# Revit family: 875-00-001-DN200-1200
name_source: partatom
category: Pipe Accessories
units: mm (PartAtom-declared; Revit-internal decimal feet)

## family parameters
Always vertical = Yes
Cut with Voids When Loaded = No
Part Type = Valve - Breaks Into
Round Connector Dimension = Use Diameter
Shared = No
Work Plane-Based = No

## types (26) — shared parameters
875-0200-00-03100000 = DN200_PN10
875-0200-00-13100000 = DN200_PN16
875-0250-00-03100000 = DN250_PN10
875-0250-00-13100000 = DN250_PN16
875-0300-00-03100000 = DN300_PN10
875-0300-00-13100000 = DN300_PN16
875-0350-00-03100000 = DN350_PN10
875-0350-00-13100000 = DN350_PN16
875-0400-00-03100000 = DN400_PN10
875-0400-00-13100000 = DN400_PN16
875-0450-00-03100000 = DN450_PN10
875-0450-00-13100000 = DN450_PN16
875-0500-00-03100000 = DN500_PN10
875-0500-00-13100000 = DN500_PN16
875-0600-00-03100000 = DN600_PN10
875-0600-00-13100000 = DN600_PN16
875-0700-00-03100000 = DN700_PN10
875-0700-00-13100000 = DN700_PN16
875-0800-00-03100000 = DN800_PN10
875-0800-00-13100000 = DN800_PN16
875-0900-00-03100000 = DN900_PN10
875-0900-00-13100000 = DN900_PN16
875-1000-00-03100000 = DN1000_PN10
875-1000-00-13100000 = DN1000_PN16
875-1200-00-03100000 = DN1200_PN10
875-1200-00-13100000 = DN1200_PN16
Body_Wallthickness = 10 mm  [stored 0.0328084 ft]
Description_ = AVK TILTING DISC, SLANTED CHECK VALVE
Rf_Dia = 3 mm  [stored 0.00984252 ft]
Search_Table = 875-00-001-DN200-1200
URL product pages = https://www.avkvalves.com

## per-type parameters (varying)
- DN0200_PN10: A=161 mm; B=202 mm; C=525 mm; Counter_weight=105 mm  [stored 0.344488 ft]; D=170 mm; D2=133 mm; DN=200 mm; DN_ref=174 mm; Disc_dia=165 mm; Disc_dia_ref=83 mm; Flange_Thickness=15 mm  [stored 0.0492126 ft]; H=460 mm; H3=345 mm; H_ref=290 mm; H_ref_2=193 mm; ID=100 mm  [stored 0.328084 ft]; ID_ref=100 mm  [stored 0.328084 ft]; L=230 mm; L1=55 mm  [stored 0.180446 ft]; L_ref=66 mm  [stored 0.216535 ft]; L_ref_2=60 mm  [stored 0.19685 ft]; L_ref_3=46 mm  [stored 0.150919 ft]; L_ref_4=66 mm  [stored 0.216535 ft]; Lever=30 mm  [stored 0.0984252 ft]; Pin=10 mm  [stored 0.0328084 ft]
- DN0200_PN16: A=161 mm; B=202 mm; C=525 mm; Counter_weight=105 mm  [stored 0.344488 ft]; D=170 mm; D2=133 mm; DN=200 mm; DN_ref=174 mm; Disc_dia=165 mm; Disc_dia_ref=83 mm; Flange_Thickness=15 mm  [stored 0.0492126 ft]; H=460 mm; H3=345 mm; H_ref=290 mm; H_ref_2=193 mm; ID=100 mm  [stored 0.328084 ft]; ID_ref=100 mm  [stored 0.328084 ft]; L=230 mm; L1=55 mm  [stored 0.180446 ft]; L_ref=66 mm  [stored 0.216535 ft]; L_ref_2=60 mm  [stored 0.19685 ft]; L_ref_3=46 mm  [stored 0.150919 ft]; L_ref_4=66 mm  [stored 0.216535 ft]; Lever=30 mm  [stored 0.0984252 ft]; Pin=10 mm  [stored 0.0328084 ft]
- DN0250_PN10: A=202 mm; B=230 mm; C=583 mm; Counter_weight=105 mm  [stored 0.344488 ft]; D=198 mm; D2=160 mm; DN=250 mm; DN_ref=217 mm; Disc_dia=210 mm; Disc_dia_ref=105 mm  [stored 0.344488 ft]; Flange_Thickness=15 mm  [stored 0.0492126 ft]; H=512 mm; H3=403 mm; H_ref=315 mm; H_ref_2=210 mm; ID=125 mm; ID_ref=125 mm; L=250 mm; L1=75 mm  [stored 0.246063 ft]; L_ref=71 mm; L_ref_2=65 mm; L_ref_3=50 mm  [stored 0.164042 ft]; L_ref_4=71 mm; Lever=30 mm  [stored 0.0984252 ft]; Pin=10 mm  [stored 0.0328084 ft]
- DN0250_PN16: A=202 mm; B=230 mm; C=583 mm; Counter_weight=105 mm  [stored 0.344488 ft]; D=203 mm; D2=160 mm; DN=250 mm; DN_ref=217 mm; Disc_dia=210 mm; Disc_dia_ref=105 mm  [stored 0.344488 ft]; Flange_Thickness=15 mm  [stored 0.0492126 ft]; H=512 mm; H3=408 mm; H_ref=310 mm; H_ref_2=206 mm; ID=125 mm; ID_ref=125 mm; L=250 mm; L1=75 mm  [stored 0.246063 ft]; L_ref=71 mm; L_ref_2=65 mm; L_ref_3=50 mm  [stored 0.164042 ft]; L_ref_4=71 mm; Lever=30 mm  [stored 0.0984252 ft]; Pin=10 mm  [stored 0.0328084 ft]
- DN0300_PN10: A=220 mm; B=265 mm; C=667 mm; Counter_weight=140 mm; D=223 mm; D2=185 mm; DN=300 mm; DN_ref=261 mm; Disc_dia=250 mm; Disc_dia_ref=125 mm; Flange_Thickness=20 mm  [stored 0.0656168 ft]; H=637 mm; H3=455 mm; H_ref=415 mm; H_ref_2=276 mm; ID=150 mm; ID_ref=150 mm; L=270 mm; L1=100 mm  [stored 0.328084 ft]; L_ref=77 mm; L_ref_2=70 mm  [stored 0.229659 ft]; L_ref_3=54 mm  [stored 0.177165 ft]; L_ref_4=77 mm; Lever=40 mm  [stored 0.131234 ft]; Pin=15 mm  [stored 0.0492126 ft]
- DN0300_PN16: A=220 mm; B=265 mm; C=667 mm; Counter_weight=140 mm; D=230 mm; D2=185 mm; DN=300 mm; DN_ref=261 mm; Disc_dia=250 mm; Disc_dia_ref=125 mm; Flange_Thickness=20 mm  [stored 0.0656168 ft]; H=637 mm; H3=462 mm; H_ref=407 mm; H_ref_2=271 mm; ID=150 mm; ID_ref=150 mm; L=270 mm; L1=100 mm  [stored 0.328084 ft]; L_ref=77 mm; L_ref_2=70 mm  [stored 0.229659 ft]; L_ref_3=54 mm  [stored 0.177165 ft]; L_ref_4=77 mm; Lever=40 mm  [stored 0.131234 ft]; Pin=15 mm  [stored 0.0492126 ft]
- DN0350_PN10: A=245 mm; B=300 mm; C=728 mm; Counter_weight=140 mm; D=253 mm; D2=215 mm; DN=350 mm; DN_ref=304 mm; Disc_dia=290 mm; Disc_dia_ref=145 mm; Flange_Thickness=20 mm  [stored 0.0656168 ft]; H=676 mm; H3=518 mm; H_ref=424 mm; H_ref_2=282 mm; ID=175 mm; ID_ref=175 mm; L=290 mm; L1=135 mm; L_ref=83 mm; L_ref_2=75 mm  [stored 0.246063 ft]; L_ref_3=58 mm  [stored 0.190289 ft]; L_ref_4=83 mm; Lever=40 mm  [stored 0.131234 ft]; Pin=15 mm  [stored 0.0492126 ft]
- DN0350_PN16: A=245 mm; B=300 mm; C=728 mm; Counter_weight=140 mm; D=260 mm; D2=215 mm; DN=350 mm; DN_ref=304 mm; Disc_dia=290 mm; Disc_dia_ref=145 mm; Flange_Thickness=20 mm  [stored 0.0656168 ft]; H=676 mm; H3=525 mm; H_ref=416 mm; H_ref_2=277 mm; ID=175 mm; ID_ref=175 mm; L=290 mm; L1=135 mm; L_ref=83 mm; L_ref_2=75 mm  [stored 0.246063 ft]; L_ref_3=58 mm  [stored 0.190289 ft]; L_ref_4=83 mm; Lever=40 mm  [stored 0.131234 ft]; Pin=15 mm  [stored 0.0492126 ft]
- DN0400_PN10: A=270 mm; B=345 mm; C=867 mm; Counter_weight=140 mm; D=283 mm; D2=240 mm; DN=400 mm; DN_ref=348 mm; Disc_dia=335 mm; Disc_dia_ref=168 mm; Flange_Thickness=20 mm  [stored 0.0656168 ft]; H=719 mm; H3=578 mm; H_ref=437 mm; H_ref_2=291 mm; ID=200 mm; ID_ref=200 mm; L=310 mm; L1=150 mm; L_ref=89 mm; L_ref_2=81 mm; L_ref_3=62 mm  [stored 0.203412 ft]; L_ref_4=89 mm; Lever=40 mm  [stored 0.131234 ft]; Pin=15 mm  [stored 0.0492126 ft]
- DN0400_PN16: A=270 mm; B=345 mm; C=867 mm; Counter_weight=140 mm; D=290 mm; D2=240 mm; DN=400 mm; DN_ref=348 mm; Disc_dia=335 mm; Disc_dia_ref=168 mm; Flange_Thickness=20 mm  [stored 0.0656168 ft]; H=719 mm; H3=585 mm; H_ref=429 mm; H_ref_2=286 mm; ID=200 mm; ID_ref=200 mm; L=310 mm; L1=150 mm; L_ref=89 mm; L_ref_2=81 mm; L_ref_3=62 mm  [stored 0.203412 ft]; L_ref_4=89 mm; Lever=40 mm  [stored 0.131234 ft]; Pin=15 mm  [stored 0.0492126 ft]
- DN0450_PN10: A=330 mm; B=378 mm; C=963 mm; Counter_weight=210 mm; D=308 mm; D2=265 mm; DN=450 mm; DN_ref=391 mm; Disc_dia=370 mm; Disc_dia_ref=185 mm; Flange_Thickness=30 mm  [stored 0.0984252 ft]; H=751 mm; H3=620 mm; H_ref=444 mm; H_ref_2=296 mm; ID=225 mm; ID_ref=225 mm; L=330 mm; L1=190 mm; L_ref=94 mm  [stored 0.308399 ft]; L_ref_2=86 mm  [stored 0.282152 ft]; L_ref_3=66 mm  [stored 0.216535 ft]; L_ref_4=94 mm  [stored 0.308399 ft]; Lever=60 mm  [stored 0.19685 ft]; Pin=25 mm  [stored 0.082021 ft]
- DN0450_PN16: A=330 mm; B=378 mm; C=963 mm; Counter_weight=210 mm; D=320 mm; D2=274 mm; DN=450 mm; DN_ref=391 mm; Disc_dia=370 mm; Disc_dia_ref=185 mm; Flange_Thickness=30 mm  [stored 0.0984252 ft]; H=751 mm; H3=645 mm; H_ref=431 mm; H_ref_2=287 mm; ID=225 mm; ID_ref=225 mm; L=330 mm; L1=190 mm; L_ref=94 mm  [stored 0.308399 ft]; L_ref_2=86 mm  [stored 0.282152 ft]; L_ref_3=66 mm  [stored 0.216535 ft]; L_ref_4=94 mm  [stored 0.308399 ft]; Lever=60 mm  [stored 0.19685 ft]; Pin=25 mm  [stored 0.082021 ft]
- DN0500_PN10: A=370 mm; B=405 mm; C=1006 mm; Counter_weight=210 mm; D=335 mm; D2=291 mm; DN=500 mm; DN_ref=435 mm; Disc_dia=410 mm; Disc_dia_ref=205 mm; Flange_Thickness=30 mm  [stored 0.0984252 ft]; H=809 mm; H3=675 mm; H_ref=474 mm; H_ref_2=316 mm; ID=250 mm; ID_ref=250 mm; L=350 mm; L1=210 mm; L_ref=100 mm  [stored 0.328084 ft]; L_ref_2=91 mm; L_ref_3=70 mm  [stored 0.229659 ft]; L_ref_4=100 mm  [stored 0.328084 ft]; Lever=60 mm  [stored 0.19685 ft]; Pin=25 mm  [stored 0.082021 ft]
- DN0500_PN16: A=370 mm; B=405 mm; C=1006 mm; Counter_weight=210 mm; D=358 mm; D2=305 mm; DN=500 mm; DN_ref=435 mm; Disc_dia=410 mm; Disc_dia_ref=205 mm; Flange_Thickness=30 mm  [stored 0.0984252 ft]; H=809 mm; H3=720 mm; H_ref=452 mm; H_ref_2=301 mm; ID=250 mm; ID_ref=250 mm; L=350 mm; L1=210 mm; L_ref=100 mm  [stored 0.328084 ft]; L_ref_2=91 mm; L_ref_3=70 mm  [stored 0.229659 ft]; L_ref_4=100 mm  [stored 0.328084 ft]; Lever=60 mm  [stored 0.19685 ft]; Pin=25 mm  [stored 0.082021 ft]
- DN0600_PN10: A=395 mm; B=465 mm; C=1180 mm; Counter_weight=210 mm; D=390 mm; D2=341 mm; DN=600 mm; DN_ref=522 mm; Disc_dia=500 mm; Disc_dia_ref=250 mm; Flange_Thickness=30 mm  [stored 0.0984252 ft]; H=1096 mm; H3=785 mm; H_ref=706 mm; H_ref_2=471 mm; ID=300 mm; ID_ref=300 mm; L=390 mm; L1=265 mm; L_ref=111 mm; L_ref_2=101 mm; L_ref_3=78 mm  [stored 0.255906 ft]; L_ref_4=111 mm; Lever=60 mm  [stored 0.19685 ft]; Pin=25 mm  [stored 0.082021 ft]
- DN0600_PN16: A=395 mm; B=465 mm; C=1180 mm; Counter_weight=210 mm; D=420 mm; D2=360 mm; DN=600 mm; DN_ref=522 mm; Disc_dia=500 mm; Disc_dia_ref=250 mm; Flange_Thickness=30 mm  [stored 0.0984252 ft]; H=1096 mm; H3=845 mm; H_ref=676 mm; H_ref_2=451 mm; ID=300 mm; ID_ref=300 mm; L=390 mm; L1=265 mm; L_ref=111 mm; L_ref_2=101 mm; L_ref_3=78 mm  [stored 0.255906 ft]; L_ref_4=111 mm; Lever=60 mm  [stored 0.19685 ft]; Pin=25 mm  [stored 0.082021 ft]
- DN0700_PN10: A=480 mm; B=515 mm; C=1258 mm; Counter_weight=280 mm; D=448 mm; D2=397 mm; DN=700 mm; DN_ref=609 mm; Disc_dia=580 mm; Disc_dia_ref=290 mm; Flange_Thickness=40 mm  [stored 0.131234 ft]; H=1161 mm; H3=903 mm; H_ref=714 mm; H_ref_2=476 mm; ID=350 mm; ID_ref=350 mm; L=430 mm; L1=320 mm; L_ref=123 mm; L_ref_2=112 mm; L_ref_3=86 mm  [stored 0.282152 ft]; L_ref_4=123 mm; Lever=80 mm  [stored 0.262467 ft]; Pin=35 mm  [stored 0.114829 ft]
- DN0700_PN16: A=480 mm; B=515 mm; C=1258 mm; Counter_weight=280 mm; D=455 mm; D2=397 mm; DN=700 mm; DN_ref=609 mm; Disc_dia=580 mm; Disc_dia_ref=290 mm; Flange_Thickness=40 mm  [stored 0.131234 ft]; H=1161 mm; H3=915 mm; H_ref=706 mm; H_ref_2=471 mm; ID=350 mm; ID_ref=350 mm; L=430 mm; L1=320 mm; L_ref=123 mm; L_ref_2=112 mm; L_ref_3=86 mm  [stored 0.282152 ft]; L_ref_4=123 mm; Lever=80 mm  [stored 0.262467 ft]; Pin=35 mm  [stored 0.114829 ft]
- DN0800_PN10: A=530 mm; B=560 mm; C=1377 mm; Counter_weight=280 mm; D=508 mm; D2=451 mm; DN=800 mm; DN_ref=696 mm; Disc_dia=665 mm; Disc_dia_ref=333 mm; Flange_Thickness=40 mm  [stored 0.131234 ft]; H=1241 mm; H3=1023 mm; H_ref=734 mm; H_ref_2=489 mm; ID=400 mm; ID_ref=400 mm; L=470 mm; L1=380 mm; L_ref=134 mm; L_ref_2=122 mm; L_ref_3=94 mm  [stored 0.308399 ft]; L_ref_4=134 mm; Lever=80 mm  [stored 0.262467 ft]; Pin=35 mm  [stored 0.114829 ft]
- DN0800_PN16: A=530 mm; B=560 mm; C=1377 mm; Counter_weight=280 mm; D=513 mm; D2=451 mm; DN=800 mm; DN_ref=696 mm; Disc_dia=665 mm; Disc_dia_ref=333 mm; Flange_Thickness=40 mm  [stored 0.131234 ft]; H=1241 mm; H3=1034 mm; H_ref=729 mm; H_ref_2=486 mm; ID=400 mm; ID_ref=400 mm; L=470 mm; L1=380 mm; L_ref=134 mm; L_ref_2=122 mm; L_ref_3=94 mm  [stored 0.308399 ft]; L_ref_4=134 mm; Lever=80 mm  [stored 0.262467 ft]; Pin=35 mm  [stored 0.114829 ft]
- DN0900_PN10: A=600 mm; B=628 mm; C=1515 mm; Counter_weight=315 mm; D=558 mm; D2=501 mm; DN=900 mm; DN_ref=783 mm; Disc_dia=750 mm; Disc_dia_ref=375 mm; Flange_Thickness=45 mm  [stored 0.147638 ft]; H=1460 mm; H3=1123 mm; H_ref=903 mm; H_ref_2=602 mm; ID=450 mm; ID_ref=450 mm; L=510 mm; L1=420 mm; L_ref=146 mm; L_ref_2=132 mm; L_ref_3=102 mm; L_ref_4=146 mm; Lever=90 mm  [stored 0.295276 ft]; Pin=40 mm  [stored 0.131234 ft]
- DN0900_PN16: A=600 mm; B=628 mm; C=1515 mm; Counter_weight=315 mm; D=563 mm; D2=501 mm; DN=900 mm; DN_ref=783 mm; Disc_dia=750 mm; Disc_dia_ref=375 mm; Flange_Thickness=45 mm  [stored 0.147638 ft]; H=1460 mm; H3=1183 mm; H_ref=898 mm; H_ref_2=598 mm; ID=450 mm; ID_ref=450 mm; L=510 mm; L1=420 mm; L_ref=146 mm; L_ref_2=132 mm; L_ref_3=102 mm; L_ref_4=146 mm; Lever=90 mm  [stored 0.295276 ft]; Pin=40 mm  [stored 0.131234 ft]
- DN1000_PN10: A=665 mm; B=730 mm; C=1812 mm; Counter_weight=350 mm; D=615 mm; D2=556 mm; DN=1000 mm; DN_ref=870 mm; Disc_dia=830 mm; Disc_dia_ref=415 mm; Flange_Thickness=50 mm  [stored 0.164042 ft]; H=1633 mm; H3=1240 mm; H_ref=1018 mm; H_ref_2=679 mm; ID=500 mm; ID_ref=500 mm; L=550 mm; L1=470 mm; L_ref=157 mm; L_ref_2=143 mm; L_ref_3=110 mm  [stored 0.360892 ft]; L_ref_4=157 mm; Lever=100 mm  [stored 0.328084 ft]; Pin=45 mm  [stored 0.147638 ft]
- DN1000_PN16: A=665 mm; B=730 mm; C=1812 mm; Counter_weight=350 mm; D=628 mm; D2=556 mm; DN=1000 mm; DN_ref=870 mm; Disc_dia=830 mm; Disc_dia_ref=415 mm; Flange_Thickness=50 mm  [stored 0.164042 ft]; H=1633 mm; H3=1265 mm; H_ref=1006 mm; H_ref_2=670 mm; ID=500 mm; ID_ref=500 mm; L=550 mm; L1=470 mm; L_ref=157 mm; L_ref_2=143 mm; L_ref_3=110 mm  [stored 0.360892 ft]; L_ref_4=157 mm; Lever=100 mm  [stored 0.328084 ft]; Pin=45 mm  [stored 0.147638 ft]
- DN1200_PN10: A=780 mm; B=860 mm; C=2071 mm; Counter_weight=420 mm; D=728 mm; D2=690 mm; DN=1200 mm; DN_ref=1043 mm; Disc_dia=1060 mm; Disc_dia_ref=530 mm; Flange_Thickness=60 mm  [stored 0.19685 ft]; H=1878 mm; H3=1470 mm; H_ref=1151 mm; H_ref_2=767 mm; ID=600 mm; ID_ref=480 mm; L=360 mm; L1=565 mm; L_ref=103 mm; L_ref_2=94 mm  [stored 0.308399 ft]; L_ref_3=72 mm  [stored 0.23622 ft]; L_ref_4=103 mm; Lever=120 mm; Pin=55 mm  [stored 0.180446 ft]
- DN1200_PN16: A=780 mm; B=860 mm; C=2071 mm; Counter_weight=420 mm; D=743 mm; D2=664 mm; DN=1200 mm; DN_ref=1044 mm; Disc_dia=1060 mm; Disc_dia_ref=530 mm; Flange_Thickness=60 mm  [stored 0.19685 ft]; H=1878 mm; H3=1485 mm; H_ref=1136 mm; H_ref_2=757 mm; ID=600 mm; ID_ref=480 mm; L=630 mm; L1=565 mm; L_ref=180 mm; L_ref_2=164 mm; L_ref_3=126 mm; L_ref_4=180 mm; Lever=120 mm; Pin=55 mm  [stored 0.180446 ft]

note: [stored X ft] marks values corroborated as IEEE doubles in the binary element streams (Revit-internal decimal feet)

## geometry (parser evidence)
native form markers: Sweep x5
no freeform markers — native parametric forms only
